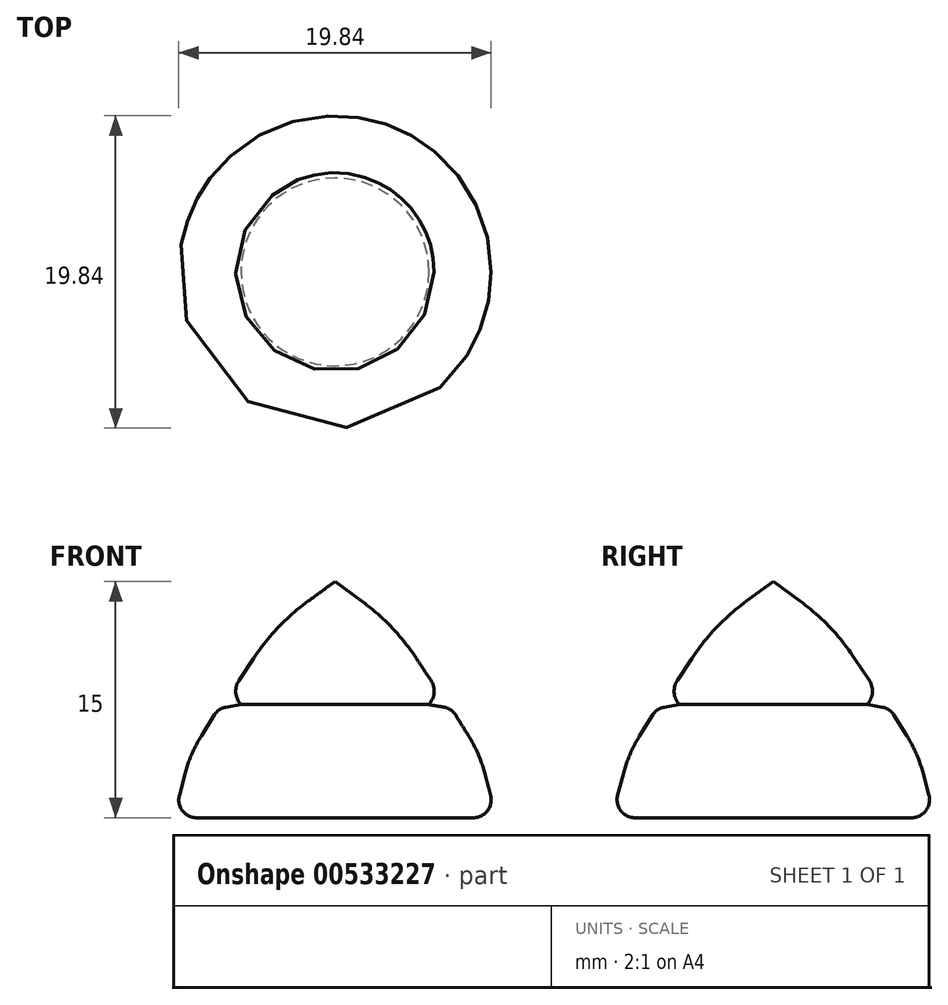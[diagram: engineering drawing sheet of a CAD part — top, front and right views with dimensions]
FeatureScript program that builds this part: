
annotation { "Feature Type Name" : "Feature", "Feature Type Description" : "" }
export const myFeature = defineFeature(function(context is Context, id is Id, definition is map)
    precondition{}
    {
        {
            var Q0;
            Q0=qCreatedBy(makeId("Front.planeOp"),FACE);
            var sketch = newSketch(context, id + "F0", { "sketchPlane" : qUnion([Q0])});
            skLineSegment(sketch, "E0", {"start": v(0, 0) * mm, "end": v(-10.26, 0) * mm});
            skLineSegment(sketch, "E1", {"start": v(-10.26, 0) * mm, "end": v(-9.19, 4.08) * mm});
            skLineSegment(sketch, "E2", {"start": v(-9.19, 4.08) * mm, "end": v(-7.4, 6.95) * mm});
            skLineSegment(sketch, "E3", {"start": v(-7.4, 6.95) * mm, "end": v(-5.96, 7.18) * mm});
            skLineSegment(sketch, "E4", {"start": v(-5.96, 7.18) * mm, "end": v(-6.56, 8.02) * mm});
            skLineSegment(sketch, "E5", {"start": v(-6.56, 8.02) * mm, "end": v(-3.76, 12.26) * mm});
            skLineSegment(sketch, "E6", {"start": v(-3.76, 12.26) * mm, "end": v(0, 15) * mm});
            skLineSegment(sketch, "E7", {"start": v(0, 15) * mm, "end": v(0, 0) * mm});
            skSolve(sketch);
        }
        {
            var Q0;
            Q0=makeQuery(id+"F0.imprint","IMPRINT",FACE,{"disambiguationData":[TD([[makeQuery(id+"F0.imprint","IMPRINT",EDGE,{"derivedFrom":sQuery(id+"F0.wireOp",EDGE,"E0")}),-1.0]])]});
            var Q1;
            Q1=sQuery(id+"F0.wireOp",EDGE,"E7");
            revolve(context, id + "F1", {"entities" : qUnion([Q0]), "axis" : qUnion([Q1]), "revolveType" : RevolveType.FULL});
        }
        {
            var Q0;
            Q0=makeQuery(id+"F1.opRevolve","SWEPT_EDGE",EDGE,{"disambiguationData":[OSD([sQuery(id+"F0.wireOp",EDGE,"E4"),sQuery(id+"F0.wireOp",EDGE,"E5")])]});
            fillet(context, id + "F2", {"entities" : qUnion([Q0]), "radius" : 1.22 * mm, "tangentPropagation" : true, "allowEdgeOverflow" : false});
        }
        {
            var Q0;
            Q0=makeQuery(id+"F1.opRevolve","SWEPT_EDGE",EDGE,{"disambiguationData":[OSD([sQuery(id+"F0.wireOp",EDGE,"E2"),sQuery(id+"F0.wireOp",EDGE,"E3")])]});
            fillet(context, id + "F3", {"entities" : qUnion([Q0]), "radius" : 1.03 * mm, "tangentPropagation" : true, "allowEdgeOverflow" : false});
        }
        {
            var Q0;
            Q0=makeQuery(id+"F1.opRevolve","SWEPT_EDGE",EDGE,{"disambiguationData":[OSD([sQuery(id+"F0.wireOp",EDGE,"E0"),sQuery(id+"F0.wireOp",EDGE,"E1")])]});
            fillet(context, id + "F4", {"entities" : qUnion([Q0]), "radius" : 1.14 * mm, "tangentPropagation" : true, "allowEdgeOverflow" : false});
        }
        {
            var Q0;
            Q0=makeQuery(id+"F1.opRevolve","SWEPT_EDGE",EDGE,{"disambiguationData":[OSD([sQuery(id+"F0.wireOp",EDGE,"E5"),sQuery(id+"F0.wireOp",EDGE,"E6")])]});
            fillet(context, id + "F5", {"entities" : qUnion([Q0]), "radius" : 14.2 * mm, "tangentPropagation" : true, "allowEdgeOverflow" : false});
        }
        {
            var Q0;
            Q0=makeQuery(id+"F1.opRevolve","SWEPT_EDGE",EDGE,{"disambiguationData":[OSD([sQuery(id+"F0.wireOp",EDGE,"E1"),sQuery(id+"F0.wireOp",EDGE,"E2")])]});
            fillet(context, id + "F6", {"entities" : qUnion([Q0]), "radius" : 8.73 * mm, "tangentPropagation" : true, "allowEdgeOverflow" : false});
        }
    });
